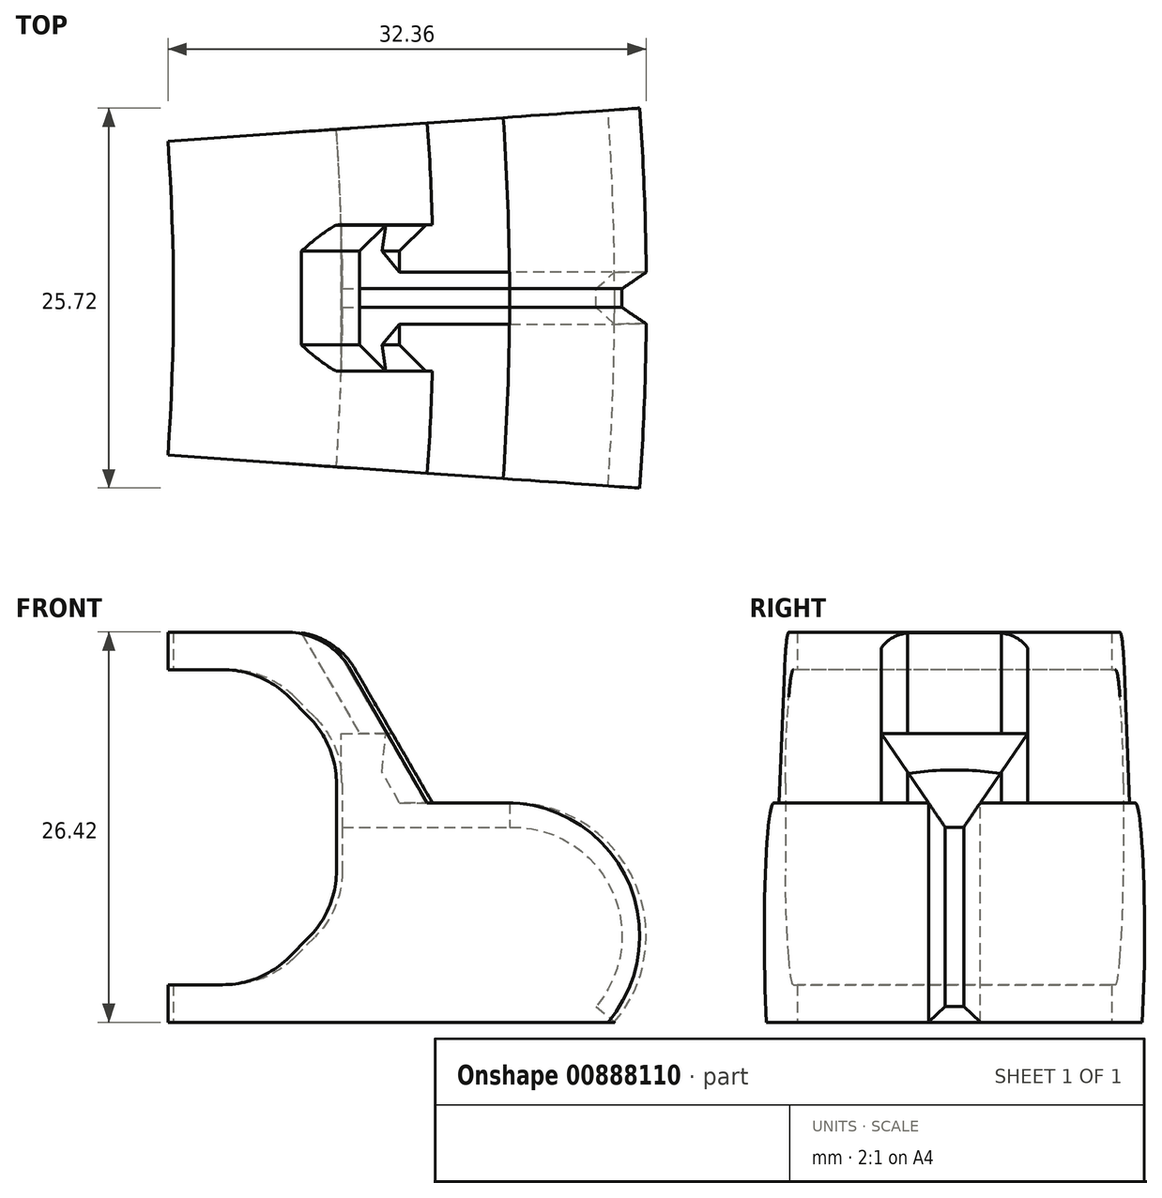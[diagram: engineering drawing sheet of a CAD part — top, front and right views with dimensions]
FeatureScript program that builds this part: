
annotation { "Feature Type Name" : "Feature", "Feature Type Description" : "" }
export const myFeature = defineFeature(function(context is Context, id is Id, definition is map)
    precondition{}
    {
        {
            var Q0;
            Q0=qCreatedBy(makeId("Front.planeOp"),FACE);
            var sketch = newSketch(context, id + "F0", { "sketchPlane" : qUnion([Q0])});
            skLineSegment(sketch, "E0", {"start": v(0, 0) * mm, "end": v(29.86, 0) * mm});
            skLineSegment(sketch, "E1", {"start": v(10.92, 26.42) * mm, "end": v(0, 26.42) * mm});
            skLineSegment(sketch, "E2", {"start": v(0, 26.42) * mm, "end": v(0, 23.88) * mm});
            skLineSegment(sketch, "E3", {"start": v(0, 23.88) * mm, "end": v(11.43, 23.88) * mm});
            skLineSegment(sketch, "E4", {"start": v(11.43, 23.88) * mm, "end": v(11.43, 2.54) * mm});
            skLineSegment(sketch, "E5", {"start": v(11.43, 2.54) * mm, "end": v(0, 2.54) * mm});
            skLineSegment(sketch, "E6", {"start": v(0, 2.54) * mm, "end": v(0, 0) * mm});
            skLineSegment(sketch, "E7", {"start": v(17.6, 14.86) * mm, "end": v(10.92, 26.42) * mm});
            skArc(sketch, "E8", {"start": v(29.86, 0) * mm, "mid": v(31.12, 9.74) * mm, "end": v(22.74, 14.86) * mm});
            skLineSegment(sketch, "E9", {"start": v(22.74, 14.86) * mm, "end": v(17.6, 14.86) * mm});
            skPoint(sketch, "E10.start.orphan", {"position": v(22.99, 0) * mm});
            skSolve(sketch);
        }
        {
            var Q0;
            Q0=qCreatedBy(makeId("Front.planeOp"),FACE);
            var sketch = newSketch(context, id + "F1", { "sketchPlane" : qUnion([Q0])});
            skLineSegment(sketch, "E11.1", {"start": v(17.6, 14.86) * mm, "end": v(10.92, 26.42) * mm});
            skSolve(sketch);
        }
        {
            var Q0;
            Q0=qCreatedBy(makeId("Top.planeOp"),FACE);
            var sketch = newSketch(context, id + "F2", { "sketchPlane" : qUnion([Q0])});
            skPoint(sketch, "E12", {"position": v(-120.8, 16.23) * mm});
            skArc(sketch, "E13", {"start": v(-0.37, -10.63) * mm, "mid": v(0, 0) * mm, "end": v(-0.37, 10.63) * mm});
            skLineSegment(sketch, "E14", {"start": v(-152.4, 0) * mm, "end": v(51.78, -14.28) * mm, "construction": true});
            skLineSegment(sketch, "E15", {"start": v(-152.4, 0) * mm, "end": v(9.98, 11.35) * mm, "construction": true});
            skSolve(sketch);
        }
        {
            var Q0;
            Q0=qCreatedBy(makeId("Right.planeOp"),FACE);
            cPlane(context, id + "F3", {"entities" : qUnion([Q0]), "cplaneType" : CPlaneType.OFFSET, "offset" : 16.5 * mm, "width" : 152.4 * mm, "height" : 152.4 * mm});
        }
        {
            var Q0;
            Q0=qCreatedBy(makeId("Front.planeOp"),FACE);
            var sketch = newSketch(context, id + "F4", { "sketchPlane" : qUnion([Q0])});
            skLineSegment(sketch, "E16.0", {"start": v(22.74, 14.86) * mm, "end": v(17.6, 14.86) * mm});
            skArc(sketch, "E16.1", {"start": v(29.86, 0) * mm, "mid": v(31.12, 9.74) * mm, "end": v(22.74, 14.86) * mm});
            skLineSegment(sketch, "E17", {"start": v(17.6, 14.86) * mm, "end": v(11.36, 14.86) * mm});
            skSolve(sketch);
        }
        {
            var Q0;
            Q0 = qSketchRegion(id + "F0", true);
            var Q1;
            Q1 = qConstructionFilter(qBodyType(qCreatedBy(id + "F2" ,EDGE), BodyType.WIRE), ConstructionObject.NO);
            sweep(context, id + "F5", {"profiles" : qUnion([Q0]), "path" : qUnion([Q1])});
        }
        {
            var Q0;
            Q0=qCreatedBy(id+"F3.planeOp",FACE);
            var sketch = newSketch(context, id + "F6", { "sketchPlane" : qUnion([Q0])});
            skLineSegment(sketch, "E18", {"start": v(4.95, 19.56) * mm, "end": v(-4.95, 19.56) * mm});
            skLineSegment(sketch, "E19", {"start": v(-4.95, 19.56) * mm, "end": v(-0.63, 13.2) * mm});
            skLineSegment(sketch, "E20", {"start": v(-0.64, 13.2) * mm, "end": v(0.64, 13.2) * mm});
            skLineSegment(sketch, "E21", {"start": v(0.64, 13.2) * mm, "end": v(4.95, 19.56) * mm});
            skSolve(sketch);
        }
        {
            var Q0;
            Q0=makeQuery(id+"F5.opSweep","SWEPT_EDGE",EDGE,{"disambiguationData":[OSD([sQuery(id+"F0.wireOp",EDGE,"E3"),sQuery(id+"F0.wireOp",EDGE,"E4"),sQuery(id+"F2.wireOp",EDGE,"XsQ3B0yG-sA46-cVKs-8mzo-xuo9gTvsWvxH")])]});
            var Q1;
            Q1=makeQuery(id+"F5.opSweep","SWEPT_EDGE",EDGE,{"disambiguationData":[OSD([sQuery(id+"F0.wireOp",EDGE,"E4"),sQuery(id+"F0.wireOp",EDGE,"E5"),sQuery(id+"F2.wireOp",EDGE,"XsQ3B0yG-sA46-cVKs-8mzo-xuo9gTvsWvxH")])]});
            chamfer(context, id + "F7", {"entities" : qUnion([Q0, Q1]), "width" : 5.08 * mm, "tangentPropagation" : true});
        }
        {
            var Q0;
            {var subQ0=sQuery(id+"F2.wireOp",EDGE,"XsQ3B0yG-sA46-cVKs-8mzo-xuo9gTvsWvxH");var subQ1=sQuery(id+"F0.wireOp",EDGE,"E4");Q0=makeQuery(id+"F7.opChamfer","BLEND_EDGE",EDGE,{"blendedFrom":[makeQuery(id+"F5.opSweep","SWEPT_EDGE",EDGE,{"disambiguationData":[OSD([subQ1,sQuery(id+"F0.wireOp",EDGE,"E5"),subQ0])]}),makeQuery(id+"F5.opSweep","SWEPT_FACE",FACE,{"disambiguationData":[OSD([subQ1,subQ0])]})],"blendedInto":[makeQuery(id+"F5.opSweep","SWEPT_FACE",FACE,{"disambiguationData":[OSD([subQ1,subQ0])]})]});}
            var Q1;
            {var subQ0=sQuery(id+"F2.wireOp",EDGE,"XsQ3B0yG-sA46-cVKs-8mzo-xuo9gTvsWvxH");var subQ1=sQuery(id+"F0.wireOp",EDGE,"E5");Q1=makeQuery(id+"F7.opChamfer","BLEND_EDGE",EDGE,{"blendedFrom":[makeQuery(id+"F5.opSweep","SWEPT_EDGE",EDGE,{"disambiguationData":[OSD([sQuery(id+"F0.wireOp",EDGE,"E4"),subQ1,subQ0])]}),makeQuery(id+"F5.opSweep","SWEPT_FACE",FACE,{"disambiguationData":[OSD([subQ1,subQ0])]})],"blendedInto":[makeQuery(id+"F5.opSweep","SWEPT_FACE",FACE,{"disambiguationData":[OSD([subQ1,subQ0])]})]});}
            var Q2;
            {var subQ0=sQuery(id+"F2.wireOp",EDGE,"XsQ3B0yG-sA46-cVKs-8mzo-xuo9gTvsWvxH");var subQ1=sQuery(id+"F0.wireOp",EDGE,"E3");Q2=makeQuery(id+"F7.opChamfer","BLEND_EDGE",EDGE,{"blendedFrom":[makeQuery(id+"F5.opSweep","SWEPT_EDGE",EDGE,{"disambiguationData":[OSD([subQ1,sQuery(id+"F0.wireOp",EDGE,"E4"),subQ0])]}),makeQuery(id+"F5.opSweep","SWEPT_FACE",FACE,{"disambiguationData":[OSD([subQ1,subQ0])]})],"blendedInto":[makeQuery(id+"F5.opSweep","SWEPT_FACE",FACE,{"disambiguationData":[OSD([subQ1,subQ0])]})]});}
            var Q3;
            {var subQ0=sQuery(id+"F2.wireOp",EDGE,"XsQ3B0yG-sA46-cVKs-8mzo-xuo9gTvsWvxH");var subQ1=sQuery(id+"F0.wireOp",EDGE,"E4");Q3=makeQuery(id+"F7.opChamfer","BLEND_EDGE",EDGE,{"blendedFrom":[makeQuery(id+"F5.opSweep","SWEPT_EDGE",EDGE,{"disambiguationData":[OSD([sQuery(id+"F0.wireOp",EDGE,"E3"),subQ1,subQ0])]}),makeQuery(id+"F5.opSweep","SWEPT_FACE",FACE,{"disambiguationData":[OSD([subQ1,subQ0])]})],"blendedInto":[makeQuery(id+"F5.opSweep","SWEPT_FACE",FACE,{"disambiguationData":[OSD([subQ1,subQ0])]})]});}
            fillet(context, id + "F8", {"entities" : qUnion([Q0, Q1, Q2, Q3]), "radius" : 6.35 * mm, "tangentPropagation" : true, "allowEdgeOverflow" : false});
        }
        {
            var Q0;
            Q0 = qSketchRegion(id + "F6", true);
            var Q1;
            Q1 = qConstructionFilter(qBodyType(qCreatedBy(id + "F6" ,EDGE), BodyType.WIRE), ConstructionObject.NO);
            var Q2;
            Q2 = qConstructionFilter(qBodyType(qCreatedBy(id + "F4" ,EDGE), BodyType.WIRE), ConstructionObject.NO);
            sweep(context, id + "F9", {"operationType" : NewBodyOperationType.REMOVE, "profiles" : qUnion([Q0]), "surfaceProfiles" : qUnion([Q1]), "path" : qUnion([Q2])});
        }
        {
            var Q0;
            Q0=makeQuery(id+"F5.opSweep","SWEPT_FACE",FACE,{"disambiguationData":[OSD([sQuery(id+"F0.wireOp",EDGE,"E1"),sQuery(id+"F2.wireOp",EDGE,"E13")])]});
            var sketch = newSketch(context, id + "F10", { "sketchPlane" : qUnion([Q0])});
            skLineSegment(sketch, "E22", {"start": v(8.64, 0) * mm, "end": v(8.64, 3.18) * mm});
            skPoint(sketch, "E22.startSnap0", {"position": v(10.92, 0) * mm});
            skLineSegment(sketch, "E23", {"start": v(8.64, 3.18) * mm, "end": v(10.4, 4.95) * mm});
            skLineSegment(sketch, "E24.MirrorCS", {"start": v(8.64, -3.18) * mm, "end": v(10.4, -4.95) * mm});
            skLineSegment(sketch, "E25.MirrorCS", {"start": v(8.64, 0) * mm, "end": v(8.64, -3.18) * mm});
            skLineSegment(sketch, "E26", {"start": v(11.18, 4.99) * mm, "end": v(11.18, -4.95) * mm});
            skLineSegment(sketch, "E27", {"start": v(10.4, 4.95) * mm, "end": v(11.18, 4.99) * mm});
            skLineSegment(sketch, "E28", {"start": v(11.18, -4.95) * mm, "end": v(10.4, -4.95) * mm});
            skSolve(sketch);
        }
        {
            var Q0;
            Q0 = qSketchRegion(id + "F10", true);
            var Q1;
            Q1 = qConstructionFilter(qBodyType(qCreatedBy(id + "F1" ,EDGE), BodyType.WIRE), ConstructionObject.NO);
            sweep(context, id + "F11", {"operationType" : NewBodyOperationType.REMOVE, "profiles" : qUnion([Q0]), "path" : qUnion([Q1])});
        }
        {
            var Q0;
            Q0=makeQuery(id+"F5.opSweep","SWEPT_EDGE",EDGE,{"disambiguationData":[OSD([sQuery(id+"F0.wireOp",EDGE,"E1"),sQuery(id+"F0.wireOp",EDGE,"E7"),sQuery(id+"F2.wireOp",EDGE,"XsQ3B0yG-sA46-cVKs-8mzo-xuo9gTvsWvxH")])]});
            fillet(context, id + "F12", {"entities" : qUnion([Q0]), "radius" : 5.08 * mm, "tangentPropagation" : true, "allowEdgeOverflow" : false});
        }
    });
